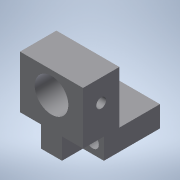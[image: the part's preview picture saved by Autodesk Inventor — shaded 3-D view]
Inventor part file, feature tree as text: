
AUTODESK INVENTOR PART (.ipt)
format: ipt  version: 2022 (Build 260153000, 153)  size: 161,280 bytes
history: native  units: mm
features: extrude x7, sketch x7, projected_geometry x4
ambient origin geometry x8: Origin, YZ Plane, XZ Plane, XY Plane, X Axis, Y Axis, Z Axis, Center Point
bodies: Solid1 (feature_tree)
feature tree (18):
  extrude  "Extrusion1"  Depth=6.0mm
  extrude  "Extrusion2"  Depth=3.5mm
  extrude  "Extrusion3"  Depth=2.8mm
  extrude  "Extrusion4"  Depth=3.2mm
  extrude  "Extrusion5"  Depth=22.0mm TaperAngle=0.0deg
  extrude  "Extrusion6"  Depth=15.0mm
  extrude  "Extrusion7"  Depth=9.6mm
  sketch  "Sketch1"  dims[d0=18.0mm d1=6.0mm]
  sketch  "Sketch2"  dims[d2=22.0mm d3=0.0mm d4=3.5mm]
  projected_geometry  "Projected Loop1"
  sketch  "Sketch3"  dims[d5=3.5mm d6=2.8mm]
  projected_geometry  "Projected Loop2"
  sketch  "Sketch4"  dims[d7=2.8mm d8=3.2mm]
  projected_geometry  "Projected Loop3"
  sketch  "Sketch5"  dims[d9=3.2mm d10=22.0mm d11=0.0mm]
  sketch  "Sketch6"  dims[d12=10.4mm d13=15.0mm]
  projected_geometry  "Projected Loop4"
  sketch  "Sketch7"  dims[d14=22.0mm d15=0.0mm d16=9.6mm d17=6.3mm d18=22.0mm d19=0.0mm d20=6.0mm d21=6.0mm d22=6.0mm d23=0.0mm d24=6.0mm d25=0.0mm d26=2.8mm d27=5.2mm d28=2.5mm d29=6.0mm d30=0.0mm]
